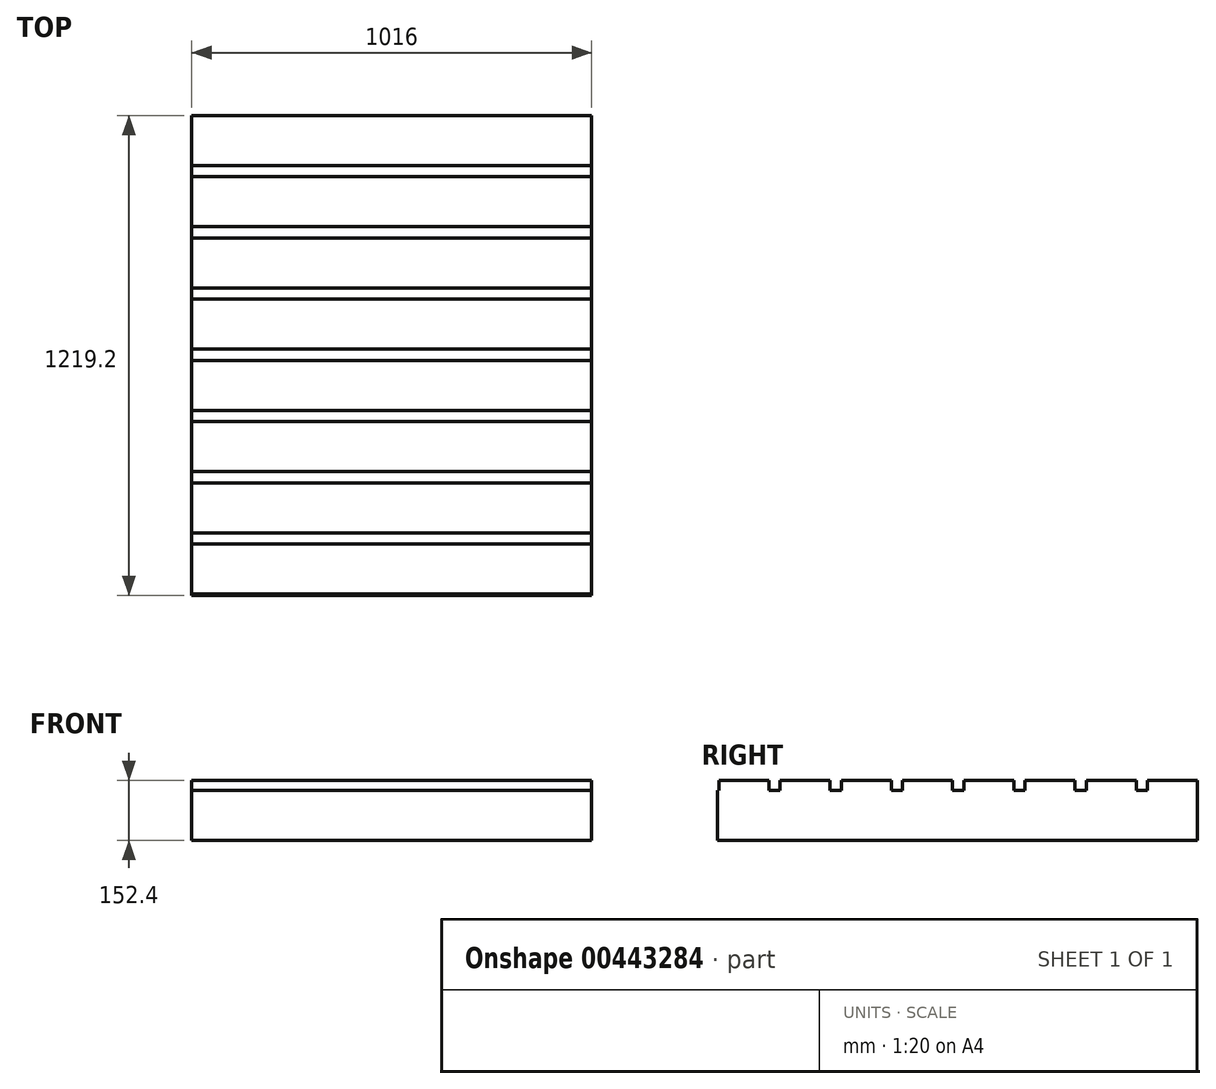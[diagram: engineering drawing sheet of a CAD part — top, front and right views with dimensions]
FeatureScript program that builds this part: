
annotation { "Feature Type Name" : "Feature", "Feature Type Description" : "" }
export const myFeature = defineFeature(function(context is Context, id is Id, definition is map)
    precondition{}
    {
        {
            var Q0;
            Q0=qCreatedBy(makeId("Top.planeOp"),FACE);
            var sketch = newSketch(context, id + "F0", { "sketchPlane" : qUnion([Q0])});
            skLineSegment(sketch, "E0.bottom", {"start": v(508, 609.6) * mm, "end": v(-508, 609.6) * mm});
            skLineSegment(sketch, "E0.top", {"start": v(508, -609.6) * mm, "end": v(-508, -609.6) * mm});
            skLineSegment(sketch, "E0.left", {"start": v(508, 609.6) * mm, "end": v(508, -609.6) * mm});
            skLineSegment(sketch, "E0.right", {"start": v(-508, 609.6) * mm, "end": v(-508, -609.6) * mm});
            skPoint(sketch, "E0.middle", {"position": v(0, 0) * mm});
            skSolve(sketch);
        }
        {
            var Q0;
            Q0 = qSketchRegion(id + "F0", true);
            extrude(context, id + "F1", {"entities" : qUnion([Q0]), "depth" : 127 * mm});
        }
        {
            var Q0;
            Q0=makeQuery(id+"F1.opExtrude","CAP_FACE",FACE,{"disambiguationData":[OSD([sQuery(id+"F0.wireOp",EDGE,"E0.bottom"),sQuery(id+"F0.wireOp",EDGE,"E0.top"),sQuery(id+"F0.wireOp",EDGE,"E0.left"),sQuery(id+"F0.wireOp",EDGE,"E0.right")])],"isStart":false});
            var sketch = newSketch(context, id + "F2", { "sketchPlane" : qUnion([Q0])});
            skLineSegment(sketch, "E1.bottom", {"start": v(-508, 609.6) * mm, "end": v(508, 609.6) * mm});
            skLineSegment(sketch, "E1.top", {"start": v(-508, 482.6) * mm, "end": v(508, 482.6) * mm});
            skLineSegment(sketch, "E1.left", {"start": v(-508, 609.6) * mm, "end": v(-508, 482.6) * mm});
            skLineSegment(sketch, "E1.right", {"start": v(508, 609.6) * mm, "end": v(508, 482.6) * mm});
            skLineSegment(sketch, "E2.0.1.0", {"start": v(-508, 454.03) * mm, "end": v(508, 454.03) * mm});
            skLineSegment(sketch, "E2.0.1.1", {"start": v(-508, 327.03) * mm, "end": v(508, 327.03) * mm});
            skLineSegment(sketch, "E2.0.1.2", {"start": v(-508, 454.03) * mm, "end": v(-508, 327.03) * mm});
            skLineSegment(sketch, "E2.0.1.3", {"start": v(508, 454.03) * mm, "end": v(508, 327.03) * mm});
            skLineSegment(sketch, "E2.0.2.0", {"start": v(-508, 298.45) * mm, "end": v(508, 298.45) * mm});
            skLineSegment(sketch, "E2.0.2.1", {"start": v(-508, 171.45) * mm, "end": v(508, 171.45) * mm});
            skLineSegment(sketch, "E2.0.2.2", {"start": v(-508, 298.45) * mm, "end": v(-508, 171.45) * mm});
            skLineSegment(sketch, "E2.0.2.3", {"start": v(508, 298.45) * mm, "end": v(508, 171.45) * mm});
            skLineSegment(sketch, "E2.0.3.0", {"start": v(-508, 142.88) * mm, "end": v(508, 142.88) * mm});
            skLineSegment(sketch, "E2.0.3.1", {"start": v(-508, 15.88) * mm, "end": v(508, 15.88) * mm});
            skLineSegment(sketch, "E2.0.3.2", {"start": v(-508, 142.88) * mm, "end": v(-508, 15.88) * mm});
            skLineSegment(sketch, "E2.0.3.3", {"start": v(508, 142.88) * mm, "end": v(508, 15.88) * mm});
            skLineSegment(sketch, "E2.0.4.0", {"start": v(-508, -12.7) * mm, "end": v(508, -12.7) * mm});
            skLineSegment(sketch, "E2.0.4.1", {"start": v(-508, -139.7) * mm, "end": v(508, -139.7) * mm});
            skLineSegment(sketch, "E2.0.4.2", {"start": v(-508, -12.7) * mm, "end": v(-508, -139.7) * mm});
            skLineSegment(sketch, "E2.0.4.3", {"start": v(508, -12.7) * mm, "end": v(508, -139.7) * mm});
            skLineSegment(sketch, "E2.0.5.0", {"start": v(-508, -168.27) * mm, "end": v(508, -168.27) * mm});
            skLineSegment(sketch, "E2.0.5.1", {"start": v(-508, -295.27) * mm, "end": v(508, -295.27) * mm});
            skLineSegment(sketch, "E2.0.5.2", {"start": v(-508, -168.27) * mm, "end": v(-508, -295.27) * mm});
            skLineSegment(sketch, "E2.0.5.3", {"start": v(508, -168.27) * mm, "end": v(508, -295.27) * mm});
            skLineSegment(sketch, "E2.0.6.0", {"start": v(-508, -323.85) * mm, "end": v(508, -323.85) * mm});
            skLineSegment(sketch, "E2.0.6.1", {"start": v(-508, -450.85) * mm, "end": v(508, -450.85) * mm});
            skLineSegment(sketch, "E2.0.6.2", {"start": v(-508, -323.85) * mm, "end": v(-508, -450.85) * mm});
            skLineSegment(sketch, "E2.0.6.3", {"start": v(508, -323.85) * mm, "end": v(508, -450.85) * mm});
            skLineSegment(sketch, "E2.0.7.0", {"start": v(-508, -479.43) * mm, "end": v(508, -479.43) * mm});
            skLineSegment(sketch, "E2.0.7.1", {"start": v(-508, -606.42) * mm, "end": v(508, -606.42) * mm});
            skLineSegment(sketch, "E2.0.7.2", {"start": v(-508, -479.43) * mm, "end": v(-508, -606.42) * mm});
            skLineSegment(sketch, "E2.0.7.3", {"start": v(508, -479.43) * mm, "end": v(508, -606.42) * mm});
            skLineSegment(sketch, "E2.direction1", {"start": v(-508, 482.6) * mm, "end": v(-482.6, 482.6) * mm, "construction": true});
            skLineSegment(sketch, "E2.direction2", {"start": v(-508, 482.6) * mm, "end": v(-508, 327.03) * mm, "construction": true});
            skSolve(sketch);
        }
        {
            var Q0;
            Q0 = qSketchRegion(id + "F2", true);
            extrude(context, id + "F3", {"entities" : qUnion([Q0]), "operationType" : NewBodyOperationType.ADD, "depth" : 25.4 * mm});
        }
    });
